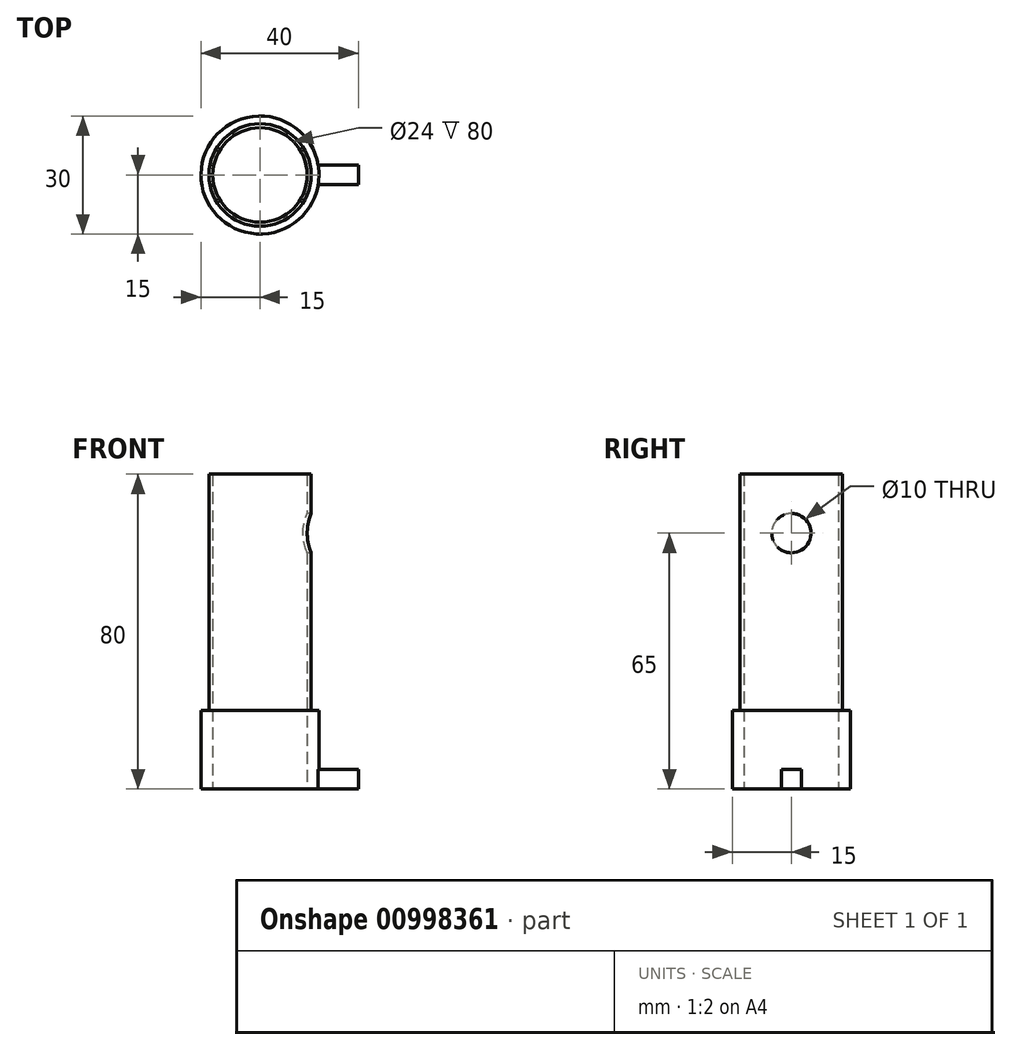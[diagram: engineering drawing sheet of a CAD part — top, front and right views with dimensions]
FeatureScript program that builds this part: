
annotation { "Feature Type Name" : "Feature", "Feature Type Description" : "" }
export const myFeature = defineFeature(function(context is Context, id is Id, definition is map)
    precondition{}
    {
        {
            var Q0;
            Q0=qCreatedBy(makeId("Top.planeOp"),FACE);
            var sketch = newSketch(context, id + "F0", { "sketchPlane" : qUnion([Q0])});
            skCircle(sketch, "E0", {"center": v(0, 0) * mm, "radius": 15 * mm});
            skCircle(sketch, "E1", {"center": v(0, 0) * mm, "radius": 12 * mm});
            skSolve(sketch);
        }
        {
            var Q0;
            Q0 = qSketchRegion(id + "F0", true);
            extrude(context, id + "F1", {"entities" : qUnion([Q0]), "depth" : 20 * mm, "offsetDistance" : 25 * mm});
        }
        {
            var Q0;
            Q0=makeQuery(id+"F1.opExtrude","CAP_FACE",FACE,{"disambiguationData":[OSD([sQuery(id+"F0.wireOp",EDGE,"E0"),sQuery(id+"F0.wireOp",EDGE,"E1")])],"isStart":false});
            var sketch = newSketch(context, id + "F2", { "sketchPlane" : qUnion([Q0])});
            skCircle(sketch, "E2.0", {"center": v(0, 0) * mm, "radius": 12 * mm});
            skCircle(sketch, "E3", {"center": v(0, 0) * mm, "radius": 13 * mm});
            skSolve(sketch);
        }
        {
            var Q0;
            Q0=makeQuery(id+"F2.imprint","IMPRINT",FACE,{"disambiguationData":[TD([[makeQuery(id+"F2.imprint","IMPRINT",EDGE,{"derivedFrom":sQuery(id+"F2.wireOp",EDGE,"E2.0")}),-1.0]])]});
            extrude(context, id + "F3", {"entities" : qUnion([Q0]), "operationType" : NewBodyOperationType.ADD, "depth" : 60 * mm, "offsetDistance" : 25 * mm});
        }
        {
            var Q0;
            Q0=qCreatedBy(makeId("Top.planeOp"),FACE);
            var sketch = newSketch(context, id + "F4", { "sketchPlane" : qUnion([Q0])});
            skCircle(sketch, "E4.0", {"center": v(0, 0) * mm, "radius": 15 * mm});
            skLineSegment(sketch, "E5", {"start": v(14.8, -2.5) * mm, "end": v(25, -2.5) * mm});
            skLineSegment(sketch, "E6", {"start": v(25, -2.5) * mm, "end": v(25, 2.5) * mm});
            skLineSegment(sketch, "E7", {"start": v(25, 2.5) * mm, "end": v(14.8, 2.5) * mm});
            skLineSegment(sketch, "E8", {"start": v(0, 0) * mm, "end": v(25, 0) * mm});
            skSolve(sketch);
        }
        {
            var Q0;
            {var subQ0=sQuery(id+"F4.wireOp",EDGE,"E5");Q0=makeQuery(id+"F4.imprint","IMPRINT",FACE,{"disambiguationData":[TD([[makeQuery(id+"F4.imprint","IMPRINT",EDGE,{"derivedFrom":subQ0}),1.0]])]});}
            var Q1;
            {var subQ0=sQuery(id+"F4.wireOp",EDGE,"E7");Q1=makeQuery(id+"F4.imprint","IMPRINT",FACE,{"disambiguationData":[TD([[makeQuery(id+"F4.imprint","IMPRINT",EDGE,{"derivedFrom":subQ0}),1.0]])]});}
            extrude(context, id + "F5", {"entities" : qUnion([Q0, Q1]), "operationType" : NewBodyOperationType.ADD, "depth" : 5 * mm, "offsetDistance" : 25 * mm});
        }
        {
            var Q0;
            Q0=qCreatedBy(makeId("Right.planeOp"),FACE);
            var sketch = newSketch(context, id + "F6", { "sketchPlane" : qUnion([Q0])});
            skLineSegment(sketch, "E9.0", {"start": v(-13, 20) * mm, "end": v(13, 20) * mm});
            skLineSegment(sketch, "E10.0", {"start": v(-13, 80) * mm, "end": v(13, 80) * mm});
            skCircle(sketch, "E11", {"center": v(0, 65) * mm, "radius": 5 * mm});
            skLineSegment(sketch, "E12", {"start": v(0, 65) * mm, "end": v(0, 20) * mm});
            skSolve(sketch);
        }
        {
            var Q0;
            Q0=makeQuery(id+"F6.imprint","IMPRINT",FACE,{"disambiguationData":[TD([[makeQuery(id+"F6.imprint","IMPRINT",EDGE,{"derivedFrom":sQuery(id+"F6.wireOp",EDGE,"E11")}),1.0]])]});
            extrude(context, id + "F7", {"entities" : qUnion([Q0]), "operationType" : NewBodyOperationType.REMOVE, "depth" : 25 * mm, "offsetDistance" : 25 * mm});
        }
    });
